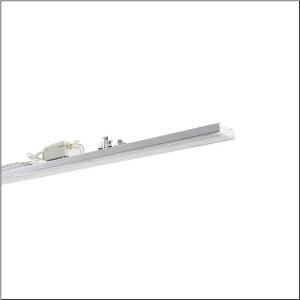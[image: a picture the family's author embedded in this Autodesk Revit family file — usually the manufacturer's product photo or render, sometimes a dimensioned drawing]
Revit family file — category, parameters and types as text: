
# Revit family: licross_r__21_recessed_ho_52te12dv4lxm_5120
name_source: partatom
category: Lighting Fixtures
units: mm (PartAtom-declared; Revit-internal decimal feet)

## family parameters
Cut with Voids When Loaded = No
Host = Face
Light Source = No
Part Type = Normal
Room Calculation Point = No
Round Connector Dimension = Use Diameter
Shared = No

## types (1)
- --- (1 x LED, 20000 lm, 109.8 W, 4000K)
    Apparent Load = 110 VA
    CIE Flux Codes = 69 91 98 100 100
    Color Rendering = 80
    Color Temperature = 4000K
    Default Elevation = 1800 mm
    Description = Licross® 21 Recessed HO, luminaire insert, of sheet steel, galvanised, coil coated, white, length: 2.250mm, width: 66mm, height: 67mm, LED rated luminous flux: 20.000lm, light colour: 840, control gear: DALI 2, with plug, 5-pole, with phase selection, mains connection: 220..240V, AC, 50/60Hz, rated input power: 110W, halogen-free wiring, primary optical cover: cover, of PMMA, light emission: direct distribution, primary light characteristic: symmetric, protection rating (complete): IP54, insulation class (complete): insulation class I (protective earthing), certification: CE, ENEC, VDE, UKCA, protection symbol: D if used in an environment with non-conductive dust loads with corresponding accessories, impact resistance: IK06, permissible ambient temperature for indoor applications: -40..+35°C, corresponds to IFS (International Featured Standards) requirements for safety and quality in the food industry, reducing of maximum allowable ambient temperature of 5°C with ceiling mounting, LABS conformity tested according to VDMA 24364:2018-05, packaging unit: 1 piece
    Height = 58 mm
    Lamp = 1 x LED
    Lamp Light Flux = 20000 lm
    Lamp Power = 109.8 W
    Lamp count = 1
    Length = 2250 mm
    Luminous efficacy = 182 lm/W
    Manufacturer = Siteco
    ModVariant = No
    Model = 52TE12DV4LXM
    Mounting Place = Ceiling
    Mounting Type = Pendant
    Number of Poles = 1
    OnlyDefault = Yes
    Power Factor = 1
    Product Name = Licross® 21 Recessed HO
    Product group = luminaire insert
    ProductGroupID = 901
    Protection Class = Protection class I
    Protection Degree = IP 54
    RLX_Detail_Level = 1
    RLX_Emergency_Light_Flux = 0 lm
    RLX_Emergency_Type = 0
    RLX_Emergency_Type_DB = No
    RlxData = <blob elided: 29373 chars, md5=81ed6cec>
    Socket = socket
    Standby Power = 0 W
    System Light Flux = 20000 lm
    System Power = 110 W
    Type Comments = factory setting: luminous flux: 100 % | dim-lin: 254 | 425 mA
    Type Image = l_1296930.jpg
    URL = http://relux.com
    VarID = @adj_046639
    Voltage = 0 V
    Weight = 0.00 kg
    Width = 66 mm

## geometry (parser evidence)
native form markers: Blend x4, Sweep x10
no freeform markers — native parametric forms only
